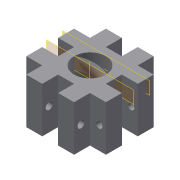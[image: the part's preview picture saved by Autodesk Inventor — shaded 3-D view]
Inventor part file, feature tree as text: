
AUTODESK INVENTOR PART (.ipt)
format: ipt  version: 2018 (Build 220112000, 112)  size: 250,880 bytes
history: native  units: mm
features: sketch x4, extrude x3, plane x2, pattern_circular x1, other x1, helix x1, fillet x1
ambient origin geometry x8: Origin, YZ Plane, XZ Plane, XY Plane, X Axis, Y Axis, Z Axis, Center Point
bodies: Solid1 (feature_tree)
feature tree (13):
  extrude  "Extrusion1"  Depth=13.0mm
  extrude  "Extrusion6"  Depth=7.0mm
  extrude  "Extrusion7"  Depth=7.0mm
  pattern_circular  "Circular Pattern3"  [2 undecoded]
  plane  "Work Plane3"
  sketch  "Sketch10"  dims[d59=7.0mm d60=7.0mm d61=7.0mm d62=90.0deg d63=7.0mm d64=7.0mm d65=90.0deg d66=7.0mm d67=7.0mm d68=7.0mm d69=7.0mm d70=7.0mm d71=7.0mm d72=7.0mm d73=7.0mm d74=7.0mm d75=7.0mm d76=7.0mm d77=90.0deg d78=13.0mm d81=10.0mm d82=0.0mm d83=3.0mm d84=3.0mm d85=10.0mm d86=0.0mm d87=40.0mm d88=360.0deg d93=7.0mm d94=14.0mm d95=7.0mm d100=2.5mm d101=5.0mm d102=25.0mm d103=15.0mm d104=10.0mm d105=0.0mm d106=90.0deg d107=90.0deg d108=0.0mm d109=0.0mm d111=2.0mm]
  other  "Work Axis1"
  helix  "Coil1"  [1 undecoded]
  fillet  "Fillet4"  [1 undecoded]
  sketch  "Sketch1"  dims[d28=20.0mm d29=0.0mm d49=13.0mm]
  sketch  "Sketch6"  dims[d55=7.0mm d56=7.0mm]
  sketch  "Sketch7"  dims[d57=7.0mm d58=7.0mm]
  plane  "Work Plane2"
note: 4 required parameter values undecoded (feature->parameter linkage not recoverable at this tier; creation-order binding heuristic only, values carry confidence <= 0.55)
